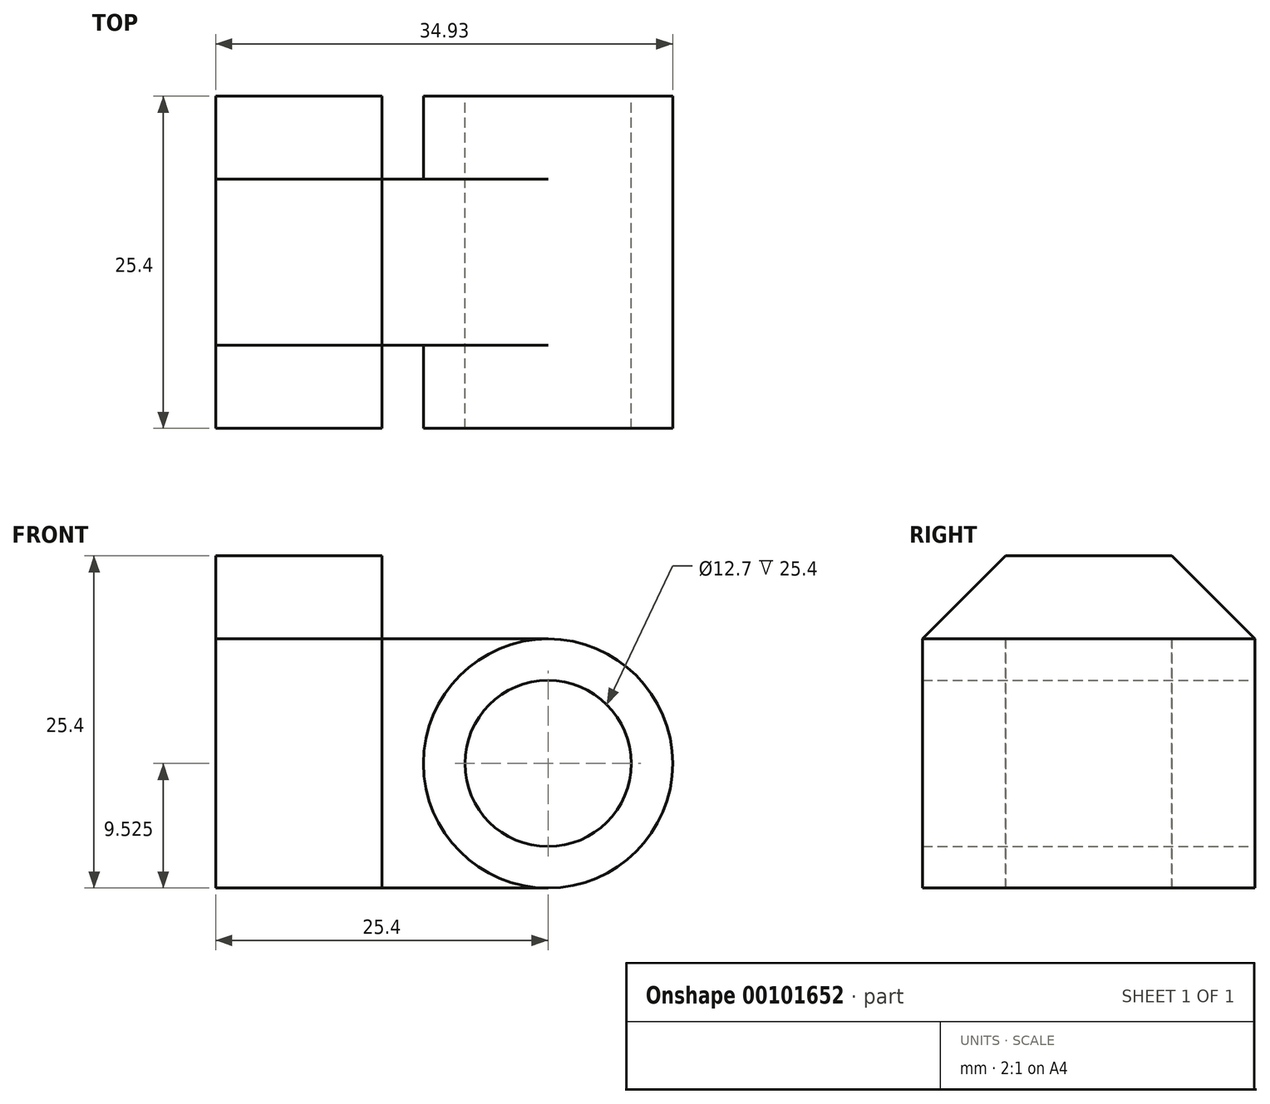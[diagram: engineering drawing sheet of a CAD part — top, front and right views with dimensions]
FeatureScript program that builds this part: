
annotation { "Feature Type Name" : "Feature", "Feature Type Description" : "" }
export const myFeature = defineFeature(function(context is Context, id is Id, definition is map)
    precondition{}
    {
        {
            var Q0;
            Q0=qCreatedBy(makeId("Right.planeOp"),FACE);
            var sketch = newSketch(context, id + "F0", { "sketchPlane" : qUnion([Q0])});
            skLineSegment(sketch, "E0", {"start": v(-12.7, 0) * mm, "end": v(0, 0) * mm});
            skLineSegment(sketch, "E1", {"start": v(0, 0) * mm, "end": v(12.7, 0) * mm});
            skLineSegment(sketch, "E2", {"start": v(12.7, 0) * mm, "end": v(12.7, 19.05) * mm});
            skLineSegment(sketch, "E3", {"start": v(12.7, 19.05) * mm, "end": v(6.35, 25.4) * mm});
            skLineSegment(sketch, "E4", {"start": v(6.35, 25.4) * mm, "end": v(-6.35, 25.4) * mm});
            skLineSegment(sketch, "E5", {"start": v(-6.35, 25.4) * mm, "end": v(-12.7, 19.05) * mm});
            skLineSegment(sketch, "E6", {"start": v(-12.7, 19.05) * mm, "end": v(-12.7, 0) * mm});
            skSolve(sketch);
        }
        {
            var Q0;
            Q0=qCreatedBy(makeId("Front.planeOp"),FACE);
            var sketch = newSketch(context, id + "F1", { "sketchPlane" : qUnion([Q0])});
            skLineSegment(sketch, "E7", {"start": v(0, 0) * mm, "end": v(0, 19.05) * mm});
            skLineSegment(sketch, "E8", {"start": v(0, 19.05) * mm, "end": v(25.4, 19.05) * mm});
            skLineSegment(sketch, "E9", {"start": v(0, 0) * mm, "end": v(25.4, 0) * mm});
            skCircle(sketch, "E10", {"center": v(25.4, 9.53) * mm, "radius": 9.53 * mm});
            skCircle(sketch, "E11", {"center": v(25.4, 9.53) * mm, "radius": 6.35 * mm});
            skSolve(sketch);
        }
        {
            var Q0;
            Q0=makeQuery(id+"F1.imprint","IMPRINT",FACE,{"disambiguationData":[TD([[makeQuery(id+"F1.imprint","IMPRINT",EDGE,{"derivedFrom":sQuery(id+"F1.wireOp",EDGE,"E11")}),-1.0]])]});
            extrude(context, id + "F2", {"entities" : qUnion([Q0]), "endBound" : BoundingType.SYMMETRIC, "depth" : 25.4 * mm});
        }
        {
            var Q0;
            Q0=makeQuery(id+"F1.imprint","IMPRINT",FACE,{"disambiguationData":[TD([[makeQuery(id+"F1.imprint","IMPRINT",EDGE,{"derivedFrom":sQuery(id+"F1.wireOp",EDGE,"E7")}),-1.0]])]});
            extrude(context, id + "F3", {"entities" : qUnion([Q0]), "operationType" : NewBodyOperationType.ADD, "endBound" : BoundingType.SYMMETRIC, "depth" : 12.7 * mm});
        }
        {
            var Q0;
            Q0=makeQuery(id+"F0.imprint","IMPRINT",FACE,{"disambiguationData":[TD([[makeQuery(id+"F0.imprint","IMPRINT",EDGE,{"derivedFrom":sQuery(id+"F0.wireOp",EDGE,"E0")}),1.0]])]});
            extrude(context, id + "F4", {"entities" : qUnion([Q0]), "operationType" : NewBodyOperationType.ADD, "depth" : 12.7 * mm});
        }
    });
